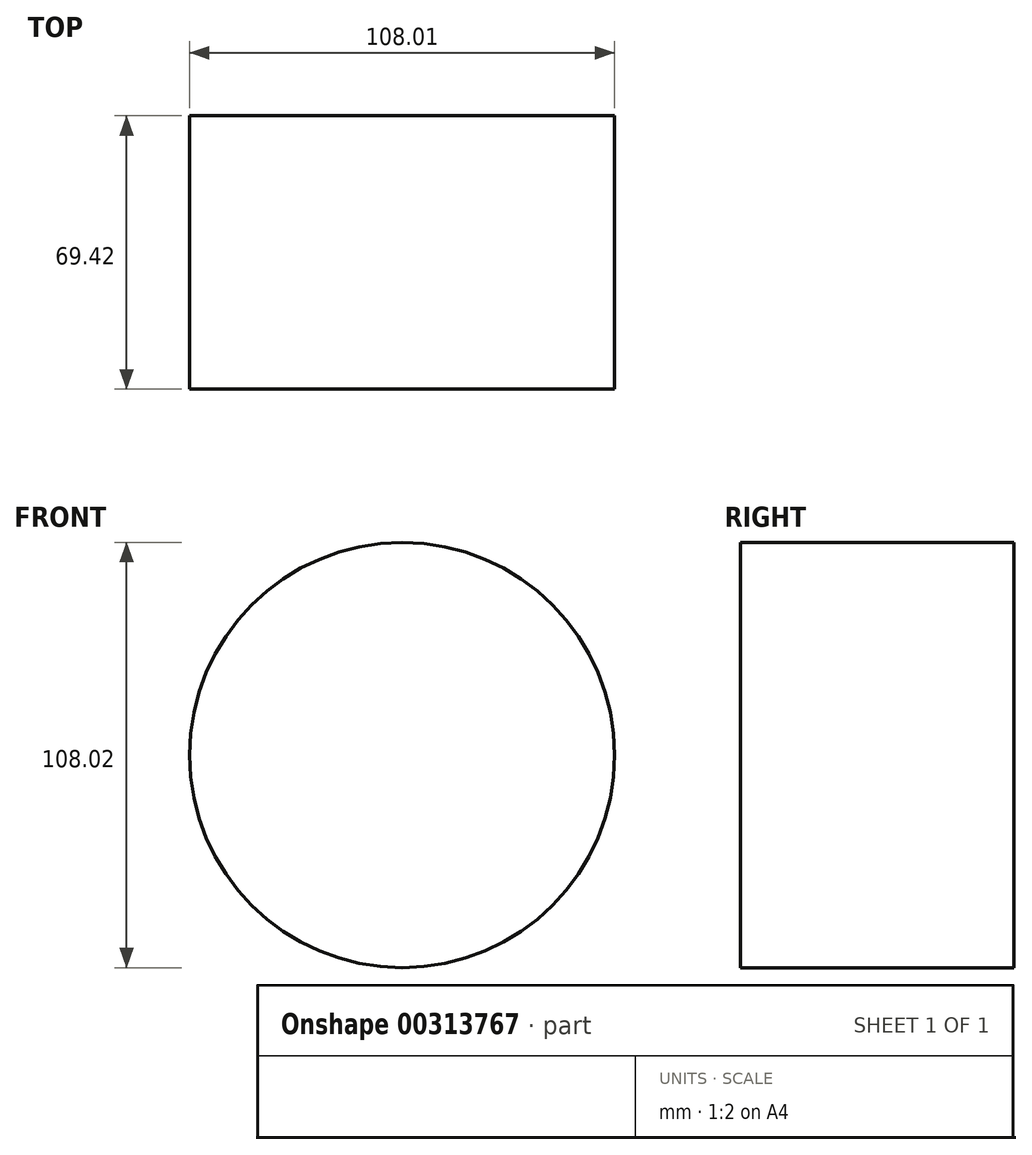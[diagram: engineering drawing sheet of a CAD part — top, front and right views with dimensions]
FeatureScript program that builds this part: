
annotation { "Feature Type Name" : "Feature", "Feature Type Description" : "" }
export const myFeature = defineFeature(function(context is Context, id is Id, definition is map)
    precondition{}
    {
        {
            var Q0;
            Q0=qCreatedBy(makeId("Front.planeOp"),FACE);
            var sketch = newSketch(context, id + "F0", { "sketchPlane" : qUnion([Q0])});
            skCircle(sketch, "E0", {"center": v(-35.65, 0) * mm, "radius": 54 * mm});
            skSolve(sketch);
        }
        {
            var Q0;
            Q0=makeQuery(id+"F0.imprint","IMPRINT",FACE,{"disambiguationData":[TD([[makeQuery(id+"F0.imprint","IMPRINT",EDGE,{"derivedFrom":sQuery(id+"F0.wireOp",EDGE,"E0")}),1.0]])]});
            extrude(context, id + "F1", {"entities" : qUnion([Q0]), "depth" : 69.42 * mm});
        }
    });
